# Revit family: Холодильные шкафы со стеклянными дверьми POLAIR Standard
name_source: partatom
category: Оборудование
units: mm (PartAtom-declared; Revit-internal decimal feet)

## family parameters
Всегда вертикально = Да
Классификация = Нет
На основе рабочей плоскости = Нет
Общий = Нет
При загрузке вырезать с полостями = Нет
Размер круглого соединителя = Использовать диаметр
Тип детали = Нормальный
Точка расчета площади = Нет

## types (17) — shared parameters
Система электропитания В/Гц = 230/50
Терморегулятор = эл.  блок
Тип охлаждения = динамический
Холодильный шкаф = <По категории>
zero-valued in all types: Отметка по умолчанию

## per-type parameters (varying)
- DB105-S: 1 дверь S=Да; 2 Корпус=Нет; 2 дверь S=Нет; Вес брутто, кг=113; Вес нетто, кг=132; Высота=1960 мм; Габаритные размеры, мм=697х710х1960; Глубина=710 мм; Дверь раздв.=Нет; Диап. рабочих температур=-21....-18; Допустимая нагрузка на полку, кг=40; Замок=+; Канапе с подсветкой=+; Кол-во полок=4; Корпус=Да; Объем, л.=500; Подсветка=вертикальная; Потребляемая мощность, Вт, не более=0,55 раб./0,40 отт.; Размер полки, мм=595*455; Размеры в упаковке, мм=744х790х2125; Расположение агрегата=верхнее; Расход электроэнергии за сутки, кВт/ч=12,5; Ручка=Да; Ручка 2.0=Нет; Тип оттайки=автомат. ТЭНами с системой исп. конденсата; Условия окр. среды (темп./вл-сть,%)=до +25/до 60; Хладагент=R404A; Цена, руб.=67 670; Ширина=697 мм; Ширина 2=600 мм; Шкаф малый 2=Нет; Шкаф малый DP=Нет
- DM110-S: 1 дверь S=Да; 2 Корпус=Да; 2 дверь S=Да; Вес брутто, кг=206; Вес нетто, кг=176; Высота=1960 мм; Габаритные размеры, мм=1402х710х1960; Глубина=710 мм; Дверь раздв.=Нет; Диап. рабочих температур=+1....+10; Допустимая нагрузка на полку, кг=40; Канапе с подсветкой=LED; Клапан Шредера=+; Кол-во полок=8; Корпус=Да; Объем, л.=1000; Подсветка=LED, вертикальная; Потребляемая мощность, Вт, не более=550; Размер полки, мм=595*455; Размеры в упаковке, мм=1490х744х2125; Расположение агрегата=верхнее; Расход электроэнергии за сутки, кВт/ч=7; Ручка=Да; Ручка 2.0=Нет; Тип оттайки=автомат. с системой исп. конденсата; Условия окр. среды (темп./вл-сть,%)=до +32/до 60; Хладагент=R134a; Цена, руб.=64 708; Ширина=1402 мм; Ширина 2=402 мм; Шкаф малый 2=Нет; Шкаф малый DP=Нет
- DM110Sd-S: 1 дверь S=Нет; 2 Корпус=Да; 2 дверь S=Нет; Вес брутто, кг=206; Вес нетто, кг=176; Высота=1960 мм; Габаритные размеры, мм=1402х710х1960; Глубина=710 мм; Дверь раздв.=Да; Диап. рабочих температур=+1....+10; Допустимая нагрузка на полку, кг=40; Канапе с подсветкой=LED; Клапан Шредера=+; Кол-во полок=8; Корпус=Да; Объем, л.=1000; Подсветка=LED, вертикальная; Потребляемая мощность, Вт, не более=550; Размер полки, мм=595*455; Размеры в упаковке, мм=1490х744х2125; Расположение агрегата=верхнее; Расход электроэнергии за сутки, кВт/ч=7; Ручка=Нет; Ручка 2.0=Нет; Тип оттайки=автомат. с системой исп. конденсата; Условия окр. среды (темп./вл-сть,%)=до +32/до 60; Хладагент=R134a; Цена, руб.=64 708; Ширина=1402 мм; Ширина 2=402 мм; Шкаф малый 2=Нет; Шкаф малый DP=Нет
- DP102-S: 1 дверь S=Нет; 2 Корпус=Нет; 2 дверь S=Нет; Вес брутто, кг=65; Вес нетто, кг=58; Высота=890 мм; Габаритные размеры, мм=600х625х890; Глубина=625 мм; Дверь раздв.=Нет; Диап. рабочих температур=-8....0; Замок=механический; Клапан Шредера=+; Кол-во полок=2; Корпус=Нет; Объем, л.=150; Подсветка=LED; Потребляемая мощность, Вт, не более=240; Размер полки, мм=505*455; Размеры в упаковке, мм=720х660х110; Расположение агрегата=нижнее; Ручка=Нет; Ручка 2.0=Нет; Тип оттайки=автомат., при помощи ТЭНов, с системой исп. конденсата; Условия окр. среды (темп./вл-сть,%)=до +32/до 60; Хладагент=R404A; Цена, руб.=35 558; Ширина=600 мм; Ширина 2=600 мм; Шкаф малый 2=Нет; Шкаф малый DP=Да
- DB102-S: 1 дверь S=Нет; 2 Корпус=Нет; 2 дверь S=Нет; Вес брутто, кг=80; Вес нетто, кг=65; Высота=870 мм; Габаритные размеры, мм=600х675х870; Глубина=675 мм; Дверь раздв.=Нет; Диап. рабочих температур=-21....-18; Допустимая нагрузка на полку, кг=40; Замок=+; Клапан Шредера=+; Кол-во полок=2+ базовая; Корпус=Нет; Объем, л.=130; Подсветка=LED верхняя; Потребляемая мощность, Вт, не более=400; Размер полки, мм=505*455; Размеры в упаковке, мм=725х795х1055; Ручка=Нет; Ручка 2.0=Нет; Тип оттайки=автомат., при помощи ТЭНов, с системой исп. конденсата; Условия окр. среды (темп./вл-сть,%)=до +25/до 60; Хладагент=R404A; Цена, руб.=47 770; Ширина=600 мм; Ширина 2=600 мм; Шкаф малый 2=Да; Шкаф малый DP=Нет
- DB107-S: 1 дверь S=Да; 2 Корпус=Нет; 2 дверь S=Нет; Вес брутто, кг=146; Вес нетто, кг=122; Высота=1960 мм; Габаритные размеры, мм=697х945х1960; Глубина=945 мм; Дверь раздв.=Нет; Диап. рабочих температур=+1....+10; Допустимая нагрузка на полку, кг=40; Замок=опция; Канапе с подсветкой=LED; Клапан Шредера=+; Кол-во полок=4; Корпус=Да; Объем, л.=700; Подсветка=LED, вертикальная; Потребляемая мощность, Вт, не более=400; Размер полки, мм=530*650; Размеры в упаковке, мм=790х988х2125; Расположение агрегата=верхнее; Расход электроэнергии за сутки, кВт/ч=5,5; Ручка=Да; Ручка 2.0=Нет; Тип оттайки=автомат. с системой исп. конденсата; Условия окр. среды (темп./вл-сть,%)=до +32/до 60; Хладагент=R404A; Цена, руб.=48 638; Ширина=697 мм; Ширина 2=600 мм; Шкаф малый 2=Нет; Шкаф малый DP=Нет
- DM105-S версия 2.0: 1 дверь S=Да; 2 Корпус=Нет; 2 дверь S=Нет; Вес брутто, кг=124; Вес нетто, кг=105; Высота=1960 мм; Габаритные размеры, мм=697х710х1960; Глубина=710 мм; Дверь раздв.=Нет; Диап. рабочих температур=+1....+10; Допустимая нагрузка на полку, кг=50; Замок=опция; Клапан Шредера=+; Кол-во полок=5; Корпус=Да; Объем, л.=500; Подсветка=LED, вертикальная; Потребляемая мощность, Вт, не более=350; Размер полки, мм=595*455; Размеры в упаковке, мм=790х744х2125; Расположение агрегата=верхнее; Расход электроэнергии за сутки, кВт/ч=2.7; Ручка=Нет; Ручка 2.0=Да; Тип оттайки=автомат. с системой исп. конденсата; Условия окр. среды (темп./вл-сть,%)=до +25/до 60; Хладагент=R134a; Цена, руб.=44 900; Ширина=697 мм; Ширина 2=600 мм; Шкаф малый 2=Нет; Шкаф малый DP=Нет
- DM105-S: 1 дверь S=Да; 2 Корпус=Нет; 2 дверь S=Нет; Вес брутто, кг=124; Вес нетто, кг=105; Высота=1960 мм; Габаритные размеры, мм=697х710х1960; Глубина=710 мм; Дверь раздв.=Нет; Диап. рабочих температур=+1....+10; Допустимая нагрузка на полку, кг=40; Замок=опция; Канапе с подсветкой=LED; Клапан Шредера=+; Кол-во полок=4; Корпус=Да; Объем, л.=500; Подсветка=LED, вертикальная; Потребляемая мощность, Вт, не более=350; Размер полки, мм=595*455; Размеры в упаковке, мм=790х744х2125; Расположение агрегата=верхнее; Расход электроэнергии за сутки, кВт/ч=4; Ручка=Да; Ручка 2.0=Нет; Тип оттайки=автомат. с системой исп. конденсата; Условия окр. среды (темп./вл-сть,%)=до +32/до 60; Хладагент=R134a; Цена, руб.=40 352; Ширина=697 мм; Ширина 2=600 мм; Шкаф малый 2=Нет; Шкаф малый DP=Нет
- DM107-S: 1 дверь S=Да; 2 Корпус=Нет; 2 дверь S=Нет; Вес брутто, кг=146; Вес нетто, кг=122; Высота=1960 мм; Габаритные размеры, мм=697х945х1960; Глубина=945 мм; Дверь раздв.=Нет; Диап. рабочих температур=+1....+10; Допустимая нагрузка на полку, кг=40; Замок=опция; Канапе с подсветкой=LED; Клапан Шредера=+; Кол-во полок=4; Корпус=Да; Объем, л.=700; Подсветка=LED, вертикальная; Потребляемая мощность, Вт, не более=400; Размер полки, мм=530*650; Размеры в упаковке, мм=790х988х2125; Расположение агрегата=верхнее; Расход электроэнергии за сутки, кВт/ч=5.5; Ручка=Да; Ручка 2.0=Нет; Тип оттайки=автомат. с системой исп. конденсата; Условия окр. среды (темп./вл-сть,%)=до +32/до 60; Хладагент=R134a; Цена, руб.=48 638; Ширина=697 мм; Ширина 2=600 мм; Шкаф малый 2=Нет; Шкаф малый DP=Нет
- DM107-S версия 2.0: 1 дверь S=Да; 2 Корпус=Нет; 2 дверь S=Нет; Вес брутто, кг=146; Вес нетто, кг=122; Высота=1960 мм; Габаритные размеры, мм=697х945х1960; Глубина=945 мм; Дверь раздв.=Нет; Диап. рабочих температур=+1....+10; Допустимая нагрузка на полку, кг=40; Замок=опция; Канапе с подсветкой=LED; Клапан Шредера=+; Кол-во полок=4; Корпус=Да; Объем, л.=700; Подсветка=LED, вертикальная; Потребляемая мощность, Вт, не более=400; Размер полки, мм=530*650; Размеры в упаковке, мм=790х988х2125; Расположение агрегата=верхнее; Расход электроэнергии за сутки, кВт/ч=3; Ручка=Нет; Ручка 2.0=Да; Тип оттайки=автомат. с системой исп. конденсата; Условия окр. среды (темп./вл-сть,%)=до +32/до 60; Хладагент=R134a; Цена, руб.=52 500; Ширина=697 мм; Ширина 2=600 мм; Шкаф малый 2=Нет; Шкаф малый DP=Нет
- DM114-S: 1 дверь S=Да; 2 Корпус=Да; 2 дверь S=Да; Вес брутто, кг=235; Вес нетто, кг=205; Высота=1960 мм; Габаритные размеры, мм=1402х945х1960; Глубина=945 мм; Дверь раздв.=Нет; Диап. рабочих температур=+1....+10; Допустимая нагрузка на полку, кг=40; Канапе с подсветкой=LED; Клапан Шредера=+; Кол-во полок=8; Корпус=Да; Объем, л.=1400; Подсветка=LED, вертикальная; Потребляемая мощность, Вт, не более=600; Размер полки, мм=595*455; Размеры в упаковке, мм=1490х988х2125; Расположение агрегата=верхнее; Расход электроэнергии за сутки, кВт/ч=8; Ручка=Да; Ручка 2.0=Нет; Тип оттайки=автомат. с системой исп. конденсата; Условия окр. среды (темп./вл-сть,%)=до +32/до 60; Хладагент=R134a; Цена, руб.=71 062; Ширина=1402 мм; Ширина 2=402 мм; Шкаф малый 2=Нет; Шкаф малый DP=Нет
- DM110Sd-S Версия 2.0: 1 дверь S=Нет; 2 Корпус=Да; 2 дверь S=Нет; Вес брутто, кг=206; Вес нетто, кг=176; Высота=1960 мм; Габаритные размеры, мм=1402х710х1960; Глубина=710 мм; Дверь раздв.=Да; Диап. рабочих температур=+1....+10; Допустимая нагрузка на полку, кг=40; Канапе с подсветкой=LED; Клапан Шредера=+; Кол-во полок=10; Корпус=Да; Объем, л.=1000; Подсветка=LED, вертикальная; Потребляемая мощность, Вт, не более=550; Размер полки, мм=645*455; Размеры в упаковке, мм=1490х744х2125; Расположение агрегата=верхнее; Расход электроэнергии за сутки, кВт/ч=7; Ручка=Нет; Ручка 2.0=Нет; Тип оттайки=автомат. с системой исп. конденсата; Условия окр. среды (темп./вл-сть,%)=до +32/до 60; Хладагент=R134a; Цена, руб.=72 270; Ширина=1402 мм; Ширина 2=402 мм; Шкаф малый 2=Нет; Шкаф малый DP=Нет
- DM114Sd-S: 1 дверь S=Нет; 2 Корпус=Да; 2 дверь S=Нет; Вес брутто, кг=235; Вес нетто, кг=205; Высота=1960 мм; Габаритные размеры, мм=1402х945х1960; Глубина=945 мм; Дверь раздв.=Да; Диап. рабочих температур=+1....+10; Допустимая нагрузка на полку, кг=40; Канапе с подсветкой=LED; Клапан Шредера=+; Кол-во полок=4; Корпус=Да; Объем, л.=1400; Подсветка=LED, вертикальная; Потребляемая мощность, Вт, не более=600; Размер полки, мм=595*455; Размеры в упаковке, мм=1490х988х2125; Расположение агрегата=верхнее; Расход электроэнергии за сутки, кВт/ч=8; Ручка=Нет; Ручка 2.0=Нет; Тип оттайки=автомат. с системой исп. конденсата; Условия окр. среды (темп./вл-сть,%)=до +32/до 60; Хладагент=R134a; Цена, руб.=71 062; Ширина=1402 мм; Ширина 2=402 мм; Шкаф малый 2=Нет; Шкаф малый DP=Нет
- DM114Sd-S Версия 2.0: 1 дверь S=Нет; 2 Корпус=Да; 2 дверь S=Нет; Вес брутто, кг=235; Вес нетто, кг=205; Высота=1960 мм; Габаритные размеры, мм=1402х945х1960; Глубина=945 мм; Дверь раздв.=Да; Диап. рабочих температур=+1....+10; Допустимая нагрузка на полку, кг=40; Канапе с подсветкой=LED; Клапан Шредера=+; Кол-во полок=10; Корпус=Да; Объем, л.=1400; Подсветка=LED, вертикальная; Потребляемая мощность, Вт, не более=600; Размер полки, мм=595*455; Размеры в упаковке, мм=1490х988х2125; Расположение агрегата=верхнее; Расход электроэнергии за сутки, кВт/ч=8; Ручка=Нет; Ручка 2.0=Нет; Тип оттайки=автомат. с системой исп. конденсата; Условия окр. среды (темп./вл-сть,%)=до +32/до 60; Хладагент=R134a; Цена, руб.=78 287; Ширина=1402 мм; Ширина 2=402 мм; Шкаф малый 2=Нет; Шкаф малый DP=Нет
- DP105-S: 1 дверь S=Да; 2 Корпус=Нет; 2 дверь S=Нет; Вес брутто, кг=124; Вес нетто, кг=105; Высота=1960 мм; Габаритные размеры, мм=697х710х1960; Глубина=710 мм; Дверь раздв.=Нет; Диап. рабочих температур=-8....0; Допустимая нагрузка на полку, кг=40; Замок=+; Канапе с подсветкой=LED; Клапан Шредера=+; Кол-во полок=4; Корпус=Да; Объем, л.=500; Подсветка=LED, вертикальная; Потребляемая мощность, Вт, не более=550; Размер полки, мм=595*455; Размеры в упаковке, мм=790х744х2125; Расположение агрегата=верхнее; Расход электроэнергии за сутки, кВт/ч=10; Ручка=Да; Ручка 2.0=Нет; Тип оттайки=автомат., при помощит ТЭНов, с системой исп. конденсата; Условия окр. среды (темп./вл-сть,%)=до +32/до 60; Хладагент=R404A; Цена, руб.=52 520; Ширина=697 мм; Ширина 2=600 мм; Шкаф малый 2=Нет; Шкаф малый DP=Нет
- DP107-S: 1 дверь S=Да; 2 Корпус=Нет; 2 дверь S=Нет; Вес брутто, кг=148; Вес нетто, кг=123; Высота=1960 мм; Габаритные размеры, мм=697х945х1960; Глубина=945 мм; Дверь раздв.=Нет; Диап. рабочих температур=-8....0; Допустимая нагрузка на полку, кг=40; Замок=+; Канапе с подсветкой=LED; Клапан Шредера=+; Кол-во полок=4; Корпус=Да; Объем, л.=700; Подсветка=LED, вертикальная; Потребляемая мощность, Вт, не более=550; Размер полки, мм=595*455; Размеры в упаковке, мм=790х988х2125; Расположение агрегата=верхнее; Расход электроэнергии за сутки, кВт/ч=10; Ручка=Да; Ручка 2.0=Нет; Тип оттайки=автомат., при помощит ТЭНов, с системой исп. конденсата; Условия окр. среды (темп./вл-сть,%)=до +32/до 60; Хладагент=R404A; Цена, руб.=56 600; Ширина=697 мм; Ширина 2=600 мм; Шкаф малый 2=Нет; Шкаф малый DP=Нет
- DV110-S: 1 дверь S=Да; 2 Корпус=Да; 2 дверь S=Да; Вес брутто, кг=206; Вес нетто, кг=176; Высота=1960 мм; Габаритные размеры, мм=1402х710х1960; Глубина=710 мм; Дверь раздв.=Нет; Диап. рабочих температур=-5....+5; Допустимая нагрузка на полку, кг=40; Канапе с подсветкой=LED; Клапан Шредера=+; Кол-во полок=8; Корпус=Да; Объем, л.=1000; Подсветка=LED, вертикальная; Потребляемая мощность, Вт, не более=550; Размер полки, мм=595*455; Размеры в упаковке, мм=1490х744х2125; Расположение агрегата=верхнее; Расход электроэнергии за сутки, кВт/ч=7; Ручка=Да; Ручка 2.0=Нет; Тип оттайки=автомат., при помощи ТЭНов, с системой исп. конденсата; Условия окр. среды (темп./вл-сть,%)=до +32/до 60; Хладагент=R134a; Цена, руб.=72 000; Ширина=1402 мм; Ширина 2=402 мм; Шкаф малый 2=Нет; Шкаф малый DP=Нет
